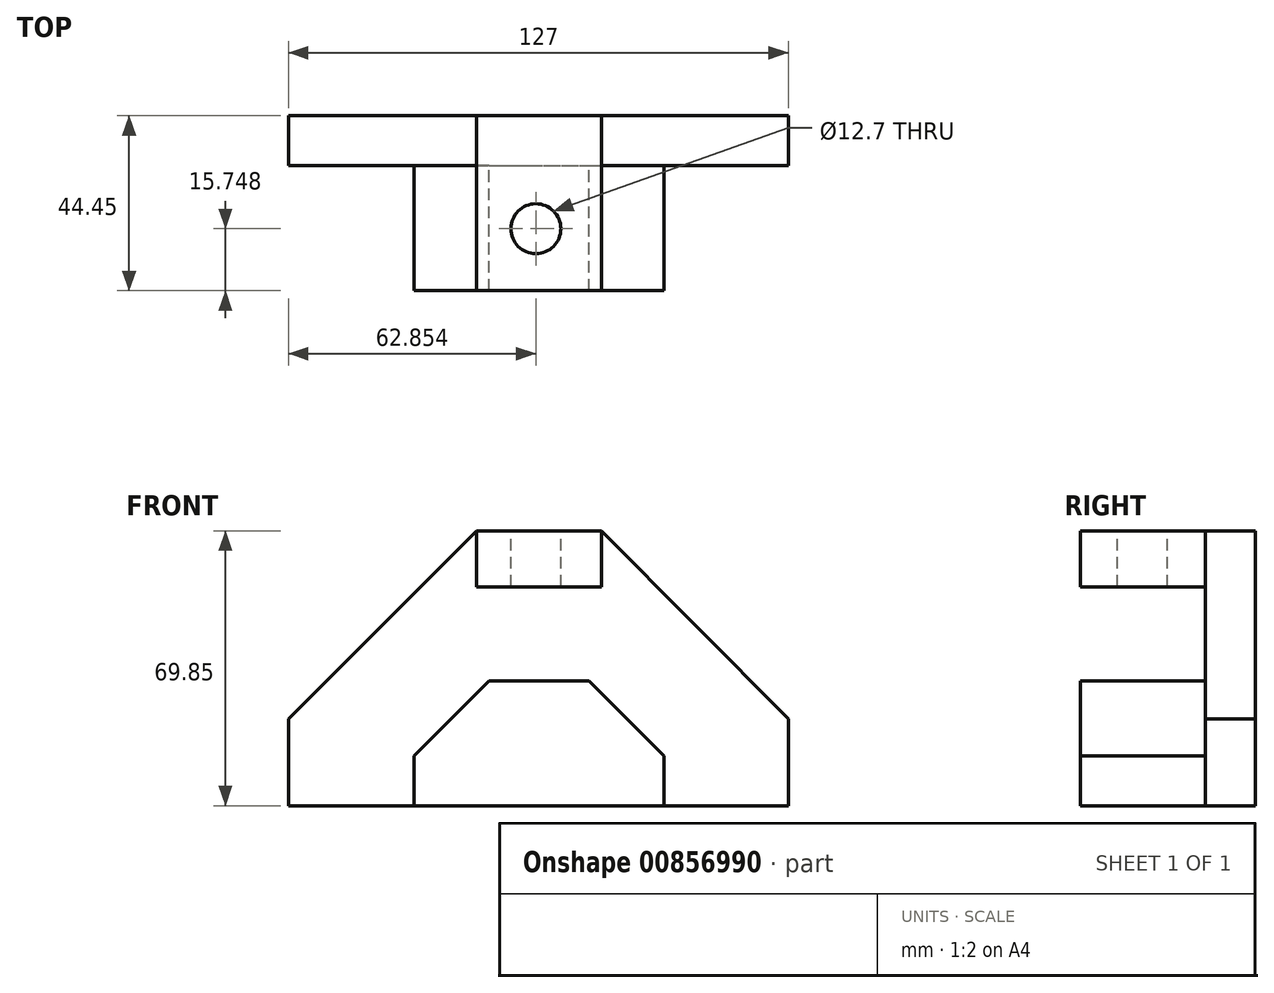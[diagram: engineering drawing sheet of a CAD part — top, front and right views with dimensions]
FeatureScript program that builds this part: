
annotation { "Feature Type Name" : "Feature", "Feature Type Description" : "" }
export const myFeature = defineFeature(function(context is Context, id is Id, definition is map)
    precondition{}
    {
        {
            var Q0;
            Q0=qCreatedBy(makeId("Front.planeOp"),FACE);
            var sketch = newSketch(context, id + "F0", { "sketchPlane" : qUnion([Q0])});
            skLineSegment(sketch, "E0", {"start": v(0, 0) * mm, "end": v(-127, 0) * mm});
            skLineSegment(sketch, "E1", {"start": v(0, 0) * mm, "end": v(0, 22.1) * mm});
            skLineSegment(sketch, "E2", {"start": v(-127, 22.1) * mm, "end": v(-127, 0) * mm});
            skLineSegment(sketch, "E3", {"start": v(0, 22.1) * mm, "end": v(-47.5, 69.85) * mm});
            skLineSegment(sketch, "E4", {"start": v(-47.5, 69.85) * mm, "end": v(-79.25, 69.85) * mm});
            skLineSegment(sketch, "E5", {"start": v(-127, 22.1) * mm, "end": v(-79.25, 69.85) * mm});
            skPoint(sketch, "E6.orphan", {"position": v(0, 69.85) * mm});
            skSolve(sketch);
        }
        {
            var Q0;
            Q0=makeQuery(id+"F0.imprint","IMPRINT",FACE,{"disambiguationData":[TD([[makeQuery(id+"F0.imprint","IMPRINT",EDGE,{"derivedFrom":sQuery(id+"F0.wireOp",EDGE,"E0")}),-1.0]])]});
            extrude(context, id + "F1", {"entities" : qUnion([Q0]), "depth" : 12.7 * mm, "offsetDistance" : 25.4 * mm});
        }
        {
            var Q0;
            Q0=makeQuery(id+"F1.opExtrude","CAP_FACE",FACE,{"disambiguationData":[OSD([sQuery(id+"F0.wireOp",EDGE,"E0"),sQuery(id+"F0.wireOp",EDGE,"E2"),sQuery(id+"F0.wireOp",EDGE,"E1"),sQuery(id+"F0.wireOp",EDGE,"E3"),sQuery(id+"F0.wireOp",EDGE,"E4"),sQuery(id+"F0.wireOp",EDGE,"E5")])],"isStart":false});
            var sketch = newSketch(context, id + "F2", { "sketchPlane" : qUnion([Q0])});
            skLineSegment(sketch, "E7", {"start": v(-31.6, 12.7) * mm, "end": v(-31.6, 0) * mm});
            skPoint(sketch, "E8.start.orphan", {"position": v(0, 11.05) * mm});
            skLineSegment(sketch, "E9", {"start": v(-95.1, 12.7) * mm, "end": v(-95.1, 0) * mm});
            skLineSegment(sketch, "E10", {"start": v(-76.04, 31.75) * mm, "end": v(-50.64, 31.75) * mm});
            skPoint(sketch, "E11.end.orphan", {"position": v(-76.04, 6.35) * mm});
            skPoint(sketch, "E11.start.orphan", {"position": v(-95.1, 6.35) * mm});
            skPoint(sketch, "E12.end.orphan", {"position": v(-50.64, 6.35) * mm});
            skPoint(sketch, "E12.start.orphan", {"position": v(-31.6, 6.35) * mm});
            skPoint(sketch, "E13.start.orphan", {"position": v(-76.04, 0) * mm});
            skPoint(sketch, "E14.orphan", {"position": v(-50.64, 0) * mm});
            skLineSegment(sketch, "E15", {"start": v(-76.04, 31.75) * mm, "end": v(-95.1, 12.7) * mm});
            skLineSegment(sketch, "E16", {"start": v(-50.64, 31.75) * mm, "end": v(-31.6, 12.7) * mm});
            skSolve(sketch);
        }
        {
            var Q0;
            Q0 = qSketchRegion(id + "F2", true);
            var Q1;
            {var subQ1=sQuery(id+"F2.wireOp",EDGE,"E7");Q1=makeQuery(id+"F2.imprint","IMPRINT",FACE,{"disambiguationData":[TD([[makeQuery(id+"F2.imprint","IMPRINT",EDGE,{"derivedFrom":subQ1}),-1.0]])]});}
            extrude(context, id + "F3", {"entities" : qUnion([Q0, Q1]), "operationType" : NewBodyOperationType.ADD, "depth" : 31.75 * mm, "offsetDistance" : 25.4 * mm});
        }
        {
            var Q0;
            Q0=makeQuery(id+"F1.opExtrude","CAP_FACE",FACE,{"disambiguationData":[OSD([sQuery(id+"F0.wireOp",EDGE,"E0"),sQuery(id+"F0.wireOp",EDGE,"E2"),sQuery(id+"F0.wireOp",EDGE,"E1"),sQuery(id+"F0.wireOp",EDGE,"E3"),sQuery(id+"F0.wireOp",EDGE,"E4"),sQuery(id+"F0.wireOp",EDGE,"E5")])],"isStart":false});
            var sketch = newSketch(context, id + "F4", { "sketchPlane" : qUnion([Q0])});
            skLineSegment(sketch, "E17", {"start": v(-79.25, 69.85) * mm, "end": v(-79.25, 55.63) * mm});
            skLineSegment(sketch, "E18", {"start": v(-79.25, 55.63) * mm, "end": v(-47.5, 55.63) * mm});
            skLineSegment(sketch, "E19", {"start": v(-47.5, 55.63) * mm, "end": v(-47.5, 69.85) * mm});
            skSolve(sketch);
        }
        {
            var Q0;
            Q0 = qSketchRegion(id + "F4", true);
            var Q1;
            Q1=makeQuery(id+"F4.imprint","IMPRINT",FACE,{"disambiguationData":[TD([[makeQuery(id+"F4.imprint","IMPRINT",EDGE,{"derivedFrom":sQuery(id+"F4.wireOp",EDGE,"E17")}),1.0]])]});
            extrude(context, id + "F5", {"entities" : qUnion([Q0, Q1]), "operationType" : NewBodyOperationType.ADD, "depth" : 31.75 * mm, "offsetDistance" : 25.4 * mm});
        }
        {
            var Q0;
            {var subQ0=sQuery(id+"F0.wireOp",EDGE,"E4");Q0=makeQuery(id+"F5.boolean.opBoolean","MERGE",FACE,{"derivedFrom":[makeQuery(id+"F1.opExtrude","SWEPT_FACE",FACE,{"disambiguationData":[OSD([subQ0])]}),makeQuery(id+"F5.opExtrude","SWEPT_FACE",FACE,{"disambiguationData":[OSD([subQ0])]})]});}
            var sketch = newSketch(context, id + "F6", { "sketchPlane" : qUnion([Q0])});
            skCircle(sketch, "E20", {"center": v(-64.15, -28.7) * mm, "radius": 6.35 * mm});
            skSolve(sketch);
        }
        {
            var Q0;
            Q0 = qSketchRegion(id + "F6", true);
            extrude(context, id + "F7", {"entities" : qUnion([Q0]), "operationType" : NewBodyOperationType.REMOVE, "oppositeDirection" : true, "depth" : 25.4 * mm, "offsetDistance" : 25.4 * mm});
        }
    });
